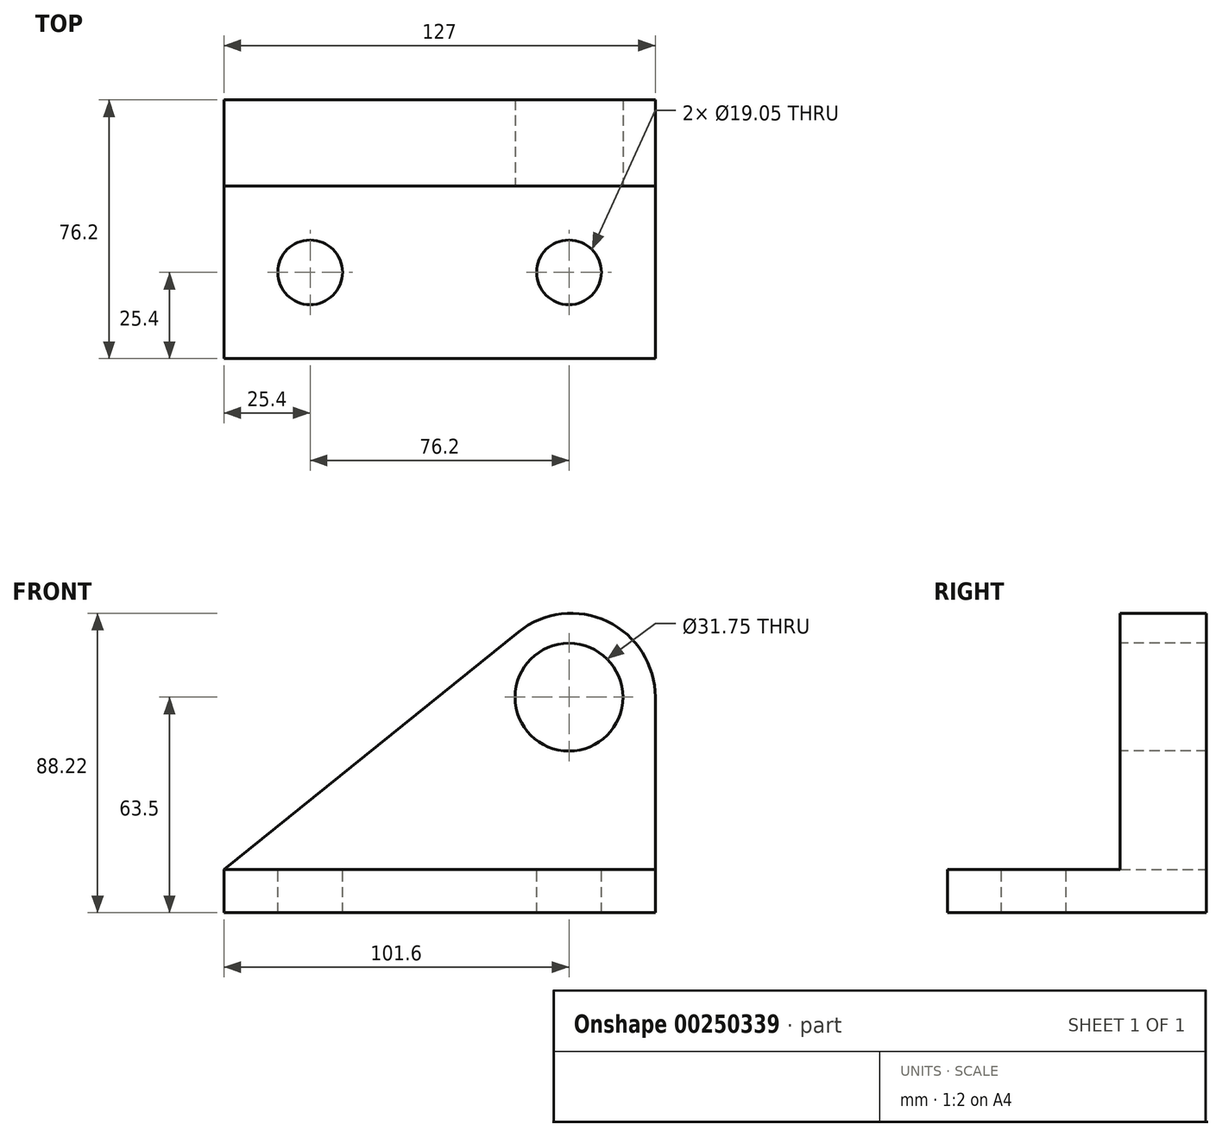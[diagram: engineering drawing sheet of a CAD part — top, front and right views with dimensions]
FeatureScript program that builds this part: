
annotation { "Feature Type Name" : "Feature", "Feature Type Description" : "" }
export const myFeature = defineFeature(function(context is Context, id is Id, definition is map)
    precondition{}
    {
        {
            var Q0;
            Q0=qCreatedBy(makeId("Front.planeOp"),FACE);
            var sketch = newSketch(context, id + "F0", { "sketchPlane" : qUnion([Q0])});
            skLineSegment(sketch, "E0", {"start": v(0, 0) * mm, "end": v(127, 0) * mm});
            skLineSegment(sketch, "E1", {"start": v(127, 0) * mm, "end": v(127, 50.8) * mm});
            skArc(sketch, "E2", {"start": v(127, 50.8) * mm, "mid": v(102.28, 75.52) * mm, "end": v(77.57, 50.8) * mm});
            skLineSegment(sketch, "E3", {"start": v(0, 0) * mm, "end": v(86.76, 70.03) * mm});
            skSolve(sketch);
        }
        {
            var Q0;
            Q0=makeQuery(id+"F0.imprint","IMPRINT",FACE,{"disambiguationData":[TD([[makeQuery(id+"F0.imprint","IMPRINT",EDGE,{"derivedFrom":sQuery(id+"F0.wireOp",EDGE,"E0")}),1.0]])]});
            extrude(context, id + "F1", {"entities" : qUnion([Q0]), "depth" : 25.4 * mm});
        }
        {
            var Q0;
            Q0=qCreatedBy(makeId("Front.planeOp"),FACE);
            var sketch = newSketch(context, id + "F2", { "sketchPlane" : qUnion([Q0])});
            skLineSegment(sketch, "E4", {"start": v(0, 0) * mm, "end": v(0, -12.7) * mm});
            skLineSegment(sketch, "E5", {"start": v(0, -12.7) * mm, "end": v(127, -12.7) * mm});
            skLineSegment(sketch, "E6", {"start": v(127, -12.7) * mm, "end": v(127, 0) * mm});
            skLineSegment(sketch, "E7", {"start": v(127, 0) * mm, "end": v(0, 0) * mm});
            skSolve(sketch);
        }
        {
            var Q0;
            Q0=makeQuery(id+"F2.imprint","IMPRINT",FACE,{"disambiguationData":[TD([[makeQuery(id+"F2.imprint","IMPRINT",EDGE,{"derivedFrom":sQuery(id+"F2.wireOp",EDGE,"E4")}),1.0]])]});
            extrude(context, id + "F3", {"entities" : qUnion([Q0]), "operationType" : NewBodyOperationType.ADD, "depth" : 76.2 * mm});
        }
        {
            var Q0;
            Q0=makeQuery(id+"F1.opExtrude","CAP_FACE",FACE,{"disambiguationData":[OSD([sQuery(id+"F0.wireOp",EDGE,"E0"),sQuery(id+"F0.wireOp",EDGE,"E1"),sQuery(id+"F0.wireOp",EDGE,"E2"),sQuery(id+"F0.wireOp",EDGE,"E3")])],"isStart":false});
            var sketch = newSketch(context, id + "F4", { "sketchPlane" : qUnion([Q0])});
            skLineSegment(sketch, "E8", {"start": v(127, 50.8) * mm, "end": v(101.6, 50.8) * mm});
            skSolve(sketch);
        }
        {
            var Q0;
            Q0=sQuery(id+"F4.wireOp",VERTEX,"E8.end");
            var Q1;
            Q1=makeQuery(id+"F1.opExtrude","SWEPT_BODY",BODY,{"disambiguationData":[OSD([sQuery(id+"F0.wireOp",EDGE,"E0"),sQuery(id+"F0.wireOp",EDGE,"E1"),sQuery(id+"F0.wireOp",EDGE,"E2"),sQuery(id+"F0.wireOp",EDGE,"E3")])]});
            hole(context, id + "F5", {"style" : HoleStyle.SIMPLE, "endStyle" : HoleEndStyle.THROUGH, "holeDiameter" : 31.75 * mm, "tappedDepth" : 12.7 * mm, "tapClearance" : 3, "locations" : qUnion([Q0]), "scope" : qUnion([Q1])});
        }
        {
            var Q0;
            Q0=makeQuery(id+"F3.opExtrude","SWEPT_FACE",FACE,{"disambiguationData":[OSD([sQuery(id+"F2.wireOp",EDGE,"E7")])]});
            var sketch = newSketch(context, id + "F6", { "sketchPlane" : qUnion([Q0])});
            skLineSegment(sketch, "E9", {"start": v(0, -50.8) * mm, "end": v(25.4, -50.8) * mm});
            skSolve(sketch);
        }
        {
            var Q0;
            Q0=sQuery(id+"F6.wireOp",VERTEX,"E9.end");
            var Q1;
            Q1=makeQuery(id+"F1.opExtrude","SWEPT_BODY",BODY,{"disambiguationData":[OSD([sQuery(id+"F0.wireOp",EDGE,"E0"),sQuery(id+"F0.wireOp",EDGE,"E1"),sQuery(id+"F0.wireOp",EDGE,"E2"),sQuery(id+"F0.wireOp",EDGE,"E3")])]});
            hole(context, id + "F7", {"style" : HoleStyle.SIMPLE, "endStyle" : HoleEndStyle.THROUGH, "holeDiameter" : 19.05 * mm, "tappedDepth" : 12.7 * mm, "tapClearance" : 3, "locations" : qUnion([Q0]), "scope" : qUnion([Q1])});
        }
        {
            var Q0;
            Q0=makeQuery(id+"F3.opExtrude","SWEPT_FACE",FACE,{"disambiguationData":[OSD([sQuery(id+"F2.wireOp",EDGE,"E7")])]});
            var sketch = newSketch(context, id + "F8", { "sketchPlane" : qUnion([Q0])});
            skLineSegment(sketch, "E10", {"start": v(127, -50.8) * mm, "end": v(101.6, -50.8) * mm});
            skSolve(sketch);
        }
        {
            var Q0;
            Q0=sQuery(id+"F8.wireOp",VERTEX,"E10.end");
            var Q1;
            Q1=makeQuery(id+"F1.opExtrude","SWEPT_BODY",BODY,{"disambiguationData":[OSD([sQuery(id+"F0.wireOp",EDGE,"E0"),sQuery(id+"F0.wireOp",EDGE,"E1"),sQuery(id+"F0.wireOp",EDGE,"E2"),sQuery(id+"F0.wireOp",EDGE,"E3")])]});
            hole(context, id + "F9", {"style" : HoleStyle.SIMPLE, "endStyle" : HoleEndStyle.THROUGH, "holeDiameter" : 19.05 * mm, "tappedDepth" : 12.7 * mm, "tapClearance" : 3, "locations" : qUnion([Q0]), "scope" : qUnion([Q1])});
        }
    });
